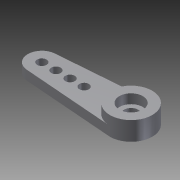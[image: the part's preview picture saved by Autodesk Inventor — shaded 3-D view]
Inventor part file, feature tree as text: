
AUTODESK INVENTOR PART (.ipt)
format: ipt  version: 2012 (Build 160160000, 160)  size: 115,200 bytes
history: native  units: mm
features: sketch x3, extrude x2, hole x1
ambient origin geometry x8: Origin, YZ Plane, XZ Plane, XY Plane, X Axis, Y Axis, Z Axis, Center Point
feature tree (6):
  sketch  "Sketch1"  dims[d3=2.0mm d7=2.0mm]
  extrude  "Extrusion9"  Depth=2.0mm
  extrude  "Extrusion10"  Depth=2.0mm
  hole  "Hole2"  [1 undecoded]
  sketch  "Sketch8"  dims[d8=2.0mm d25=3.0mm d29=2.0mm]
  sketch  "Sketch9"  dims[d30=3.0mm d33=3.0mm d47=10.0mm d48=6.0mm d50=6.0mm d51=9.0mm d52=3.0mm d53=2.0mm d54=0.0mm d55=9.0mm d56=2.0mm d57=0.0mm d58=5.0mm d59=5.0mm d60=6.0mm d61=4.0mm d62=2.0mm d63=90.0deg d64=2.0mm d65=0.0mm]
note: 1 required parameter value undecoded (feature->parameter linkage not recoverable at this tier; creation-order binding heuristic only, values carry confidence <= 0.55)
